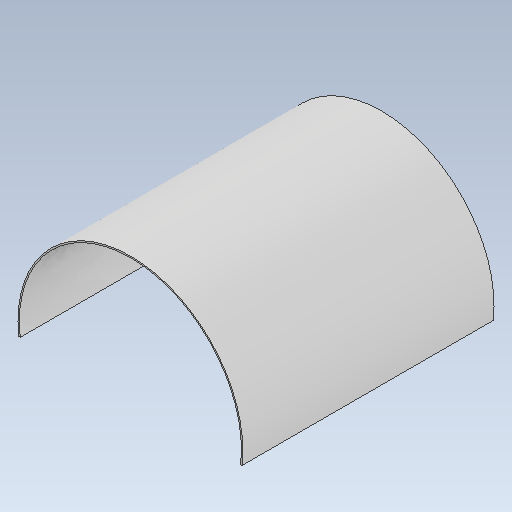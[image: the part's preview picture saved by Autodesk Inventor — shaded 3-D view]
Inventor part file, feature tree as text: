
AUTODESK INVENTOR PART (.ipt)
format: ipt  version: 2021 (Build 250183000, 183)  size: 116,736 bytes
history: native  units: mm
features: extrude x1, sketch x1
ambient origin geometry x8: Origin, YZ Plane, XZ Plane, XY Plane, X Axis, Y Axis, Z Axis, Center Point
bodies: Body1 (feature_tree)
feature tree (2):
  extrude  "shell"  Depth=10.0mm
  sketch  "Sketch2"  dims[d12=1600.0mm d13=900.0mm d14=1800.0mm d15=0.0mm d16=0.0mm d17=0.0mm d18=0.0mm d19=0.0mm d20=0.0mm d21=0.0mm d23=10.0mm]
